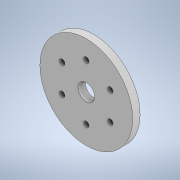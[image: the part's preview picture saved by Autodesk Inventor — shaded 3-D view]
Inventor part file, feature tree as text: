
AUTODESK INVENTOR PART (.ipt)
format: ipt  version: 2020.3 (Build 243373000, 373)  size: 120,832 bytes
history: native  units: mm
features: extrude x3, sketch x3, pattern_circular x1
ambient origin geometry x8: Origin, YZ Plane, XZ Plane, XY Plane, X Axis, Y Axis, Z Axis, Center Point
bodies: Solid1 (feature_tree)
feature tree (7):
  extrude  "Extrusion1"  Depth=4.0mm TaperAngle=0.0deg
  extrude  "Extrusion2"  Depth=15.0mm
  pattern_circular  "Circular Pattern1"  Count=6 Angle=360.0deg
  extrude  "Extrusion3"  Depth=10.0mm
  sketch  "Sketch1"  dims[d0=50.0mm d1=4.0mm d2=0.0mm]
  sketch  "Sketch2"  dims[d3=3.0mm d4=15.0mm]
  sketch  "Sketch3"  dims[d5=10.0mm d6=0.0mm d7=60.0mm d8=360.0deg d11=9.0mm d12=10.0mm d13=0.0mm]
